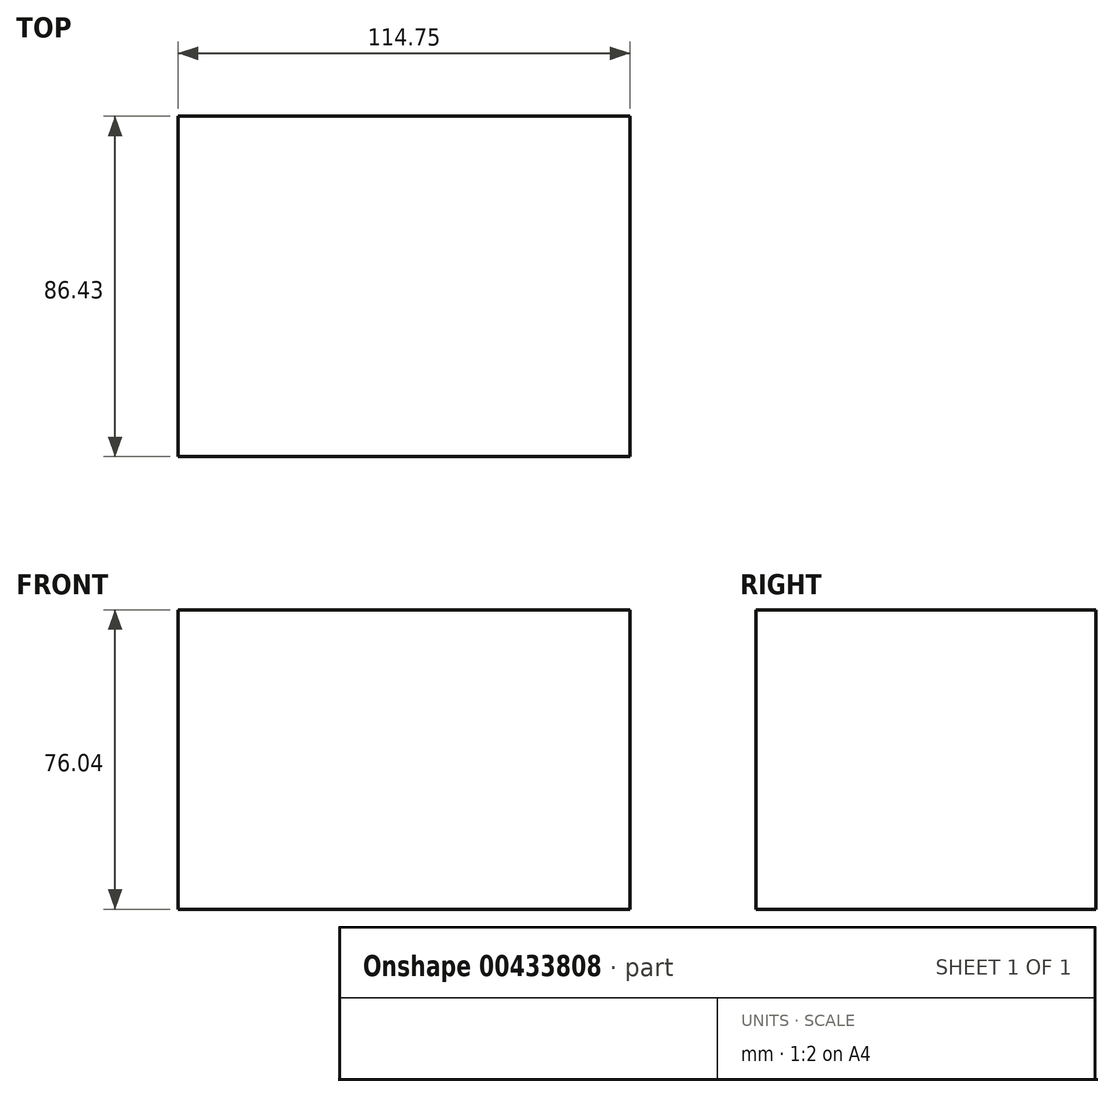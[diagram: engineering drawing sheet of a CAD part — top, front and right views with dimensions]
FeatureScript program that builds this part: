
annotation { "Feature Type Name" : "Feature", "Feature Type Description" : "" }
export const myFeature = defineFeature(function(context is Context, id is Id, definition is map)
    precondition{}
    {
        {
            var Q0;
            Q0=qCreatedBy(makeId("Top.planeOp"),FACE);
            var sketch = newSketch(context, id + "F0", { "sketchPlane" : qUnion([Q0])});
            skLineSegment(sketch, "E0.bottom", {"start": v(-54.26, 44.64) * mm, "end": v(60.5, 44.64) * mm});
            skLineSegment(sketch, "E0.top", {"start": v(-54.26, -41.8) * mm, "end": v(60.5, -41.8) * mm});
            skLineSegment(sketch, "E0.left", {"start": v(-54.26, 44.64) * mm, "end": v(-54.26, -41.8) * mm});
            skLineSegment(sketch, "E0.right", {"start": v(60.5, 44.64) * mm, "end": v(60.5, -41.8) * mm});
            skSolve(sketch);
        }
        {
            var Q0;
            Q0=makeQuery(id+"F0.imprint","IMPRINT",FACE,{"disambiguationData":[TD([[makeQuery(id+"F0.imprint","IMPRINT",EDGE,{"derivedFrom":sQuery(id+"F0.wireOp",EDGE,"E0.bottom")}),-1.0]])]});
            extrude(context, id + "F1", {"entities" : qUnion([Q0]), "depth" : 76.04 * mm});
        }
    });
